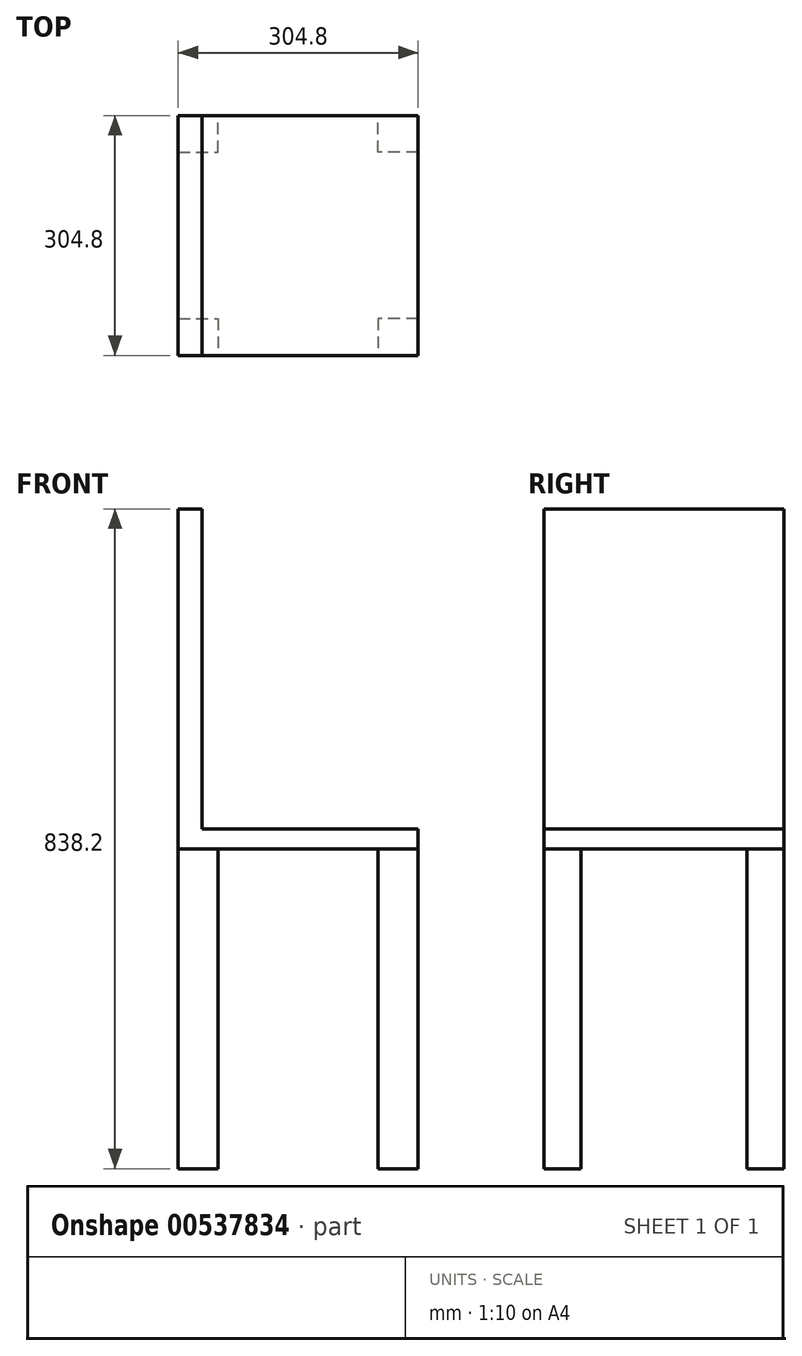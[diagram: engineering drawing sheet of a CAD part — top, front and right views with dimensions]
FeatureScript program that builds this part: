
annotation { "Feature Type Name" : "Feature", "Feature Type Description" : "" }
export const myFeature = defineFeature(function(context is Context, id is Id, definition is map)
    precondition{}
    {
        {
            var Q0;
            Q0=qCreatedBy(makeId("Top.planeOp"),FACE);
            var sketch = newSketch(context, id + "F0", { "sketchPlane" : qUnion([Q0])});
            skLineSegment(sketch, "E0", {"start": v(0, 0) * mm, "end": v(0, 46.95) * mm});
            skLineSegment(sketch, "E1", {"start": v(0, 46.95) * mm, "end": v(50.8, 46.95) * mm});
            skLineSegment(sketch, "E2", {"start": v(50.8, 46.95) * mm, "end": v(50.8, 0) * mm});
            skLineSegment(sketch, "E3", {"start": v(50.8, 0) * mm, "end": v(0, 0) * mm});
            skLineSegment(sketch, "E4", {"start": v(50.8, 0) * mm, "end": v(254, 0) * mm});
            skLineSegment(sketch, "E5", {"start": v(152.4, 0) * mm, "end": v(152.4, 304.8) * mm});
            skLineSegment(sketch, "E6.MirrorCS", {"start": v(254, 46.95) * mm, "end": v(254, 0) * mm});
            skLineSegment(sketch, "E7.MirrorCS", {"start": v(304.8, 46.95) * mm, "end": v(254, 46.95) * mm});
            skLineSegment(sketch, "E8.MirrorCS", {"start": v(304.8, 0) * mm, "end": v(304.8, 46.95) * mm});
            skLineSegment(sketch, "E9.MirrorCS", {"start": v(254, 0) * mm, "end": v(304.8, 0) * mm});
            skLineSegment(sketch, "E10", {"start": v(152.4, 152.4) * mm, "end": v(3.12, 152.4) * mm});
            skPoint(sketch, "E10.endSnap0", {"position": v(152.4, 152.4) * mm});
            skLineSegment(sketch, "E11.MirrorCS", {"start": v(0, 257.85) * mm, "end": v(50.8, 257.85) * mm});
            skLineSegment(sketch, "E12.MirrorCS", {"start": v(0, 304.8) * mm, "end": v(0, 257.85) * mm});
            skLineSegment(sketch, "E13.MirrorCS", {"start": v(50.8, 257.85) * mm, "end": v(50.8, 304.8) * mm});
            skLineSegment(sketch, "E14.MirrorCS", {"start": v(50.8, 304.8) * mm, "end": v(0, 304.8) * mm});
            skLineSegment(sketch, "E15.MirrorCS", {"start": v(304.8, 257.85) * mm, "end": v(254, 257.85) * mm});
            skLineSegment(sketch, "E16.MirrorCS", {"start": v(254, 257.85) * mm, "end": v(254, 304.8) * mm});
            skLineSegment(sketch, "E17.MirrorCS", {"start": v(304.8, 304.8) * mm, "end": v(304.8, 257.85) * mm});
            skLineSegment(sketch, "E18.MirrorCS", {"start": v(254, 304.8) * mm, "end": v(304.8, 304.8) * mm});
            skSolve(sketch);
        }
        {
            var Q0;
            Q0 = qSketchRegion(id + "F0", true);
            extrude(context, id + "F1", {"entities" : qUnion([Q0]), "depth" : 406.4 * mm, "offsetDistance" : 25.4 * mm});
        }
        {
            var Q0;
            Q0=makeQuery(id+"F1.opExtrude","CAP_FACE",FACE,{"disambiguationData":[OSD([sQuery(id+"F0.wireOp",EDGE,"E6.MirrorCS"),sQuery(id+"F0.wireOp",EDGE,"E7.MirrorCS"),sQuery(id+"F0.wireOp",EDGE,"E8.MirrorCS"),sQuery(id+"F0.wireOp",EDGE,"E9.MirrorCS")])],"isStart":false});
            var sketch = newSketch(context, id + "F2", { "sketchPlane" : qUnion([Q0])});
            skLineSegment(sketch, "E19.bottom", {"start": v(0, 0) * mm, "end": v(304.8, 0) * mm});
            skLineSegment(sketch, "E19.top", {"start": v(0, 304.8) * mm, "end": v(304.8, 304.8) * mm});
            skLineSegment(sketch, "E19.left", {"start": v(0, 0) * mm, "end": v(0, 304.8) * mm});
            skLineSegment(sketch, "E19.right", {"start": v(304.8, 0) * mm, "end": v(304.8, 304.8) * mm});
            skSolve(sketch);
        }
        {
            var Q0;
            Q0 = qSketchRegion(id + "F2", true);
            extrude(context, id + "F3", {"entities" : qUnion([Q0]), "depth" : 25.4 * mm, "offsetDistance" : 25.4 * mm});
        }
        {
            var Q0;
            Q0=makeQuery(id+"F3.opExtrude","CAP_FACE",FACE,{"disambiguationData":[OSD([sQuery(id+"F2.wireOp",EDGE,"E19.bottom"),sQuery(id+"F2.wireOp",EDGE,"E19.top"),sQuery(id+"F2.wireOp",EDGE,"E19.left"),sQuery(id+"F2.wireOp",EDGE,"E19.right")])],"isStart":false});
            var sketch = newSketch(context, id + "F4", { "sketchPlane" : qUnion([Q0])});
            skLineSegment(sketch, "E20.bottom", {"start": v(0, 0) * mm, "end": v(30.08, 0) * mm});
            skLineSegment(sketch, "E20.top", {"start": v(0, 304.8) * mm, "end": v(30.08, 304.8) * mm});
            skLineSegment(sketch, "E20.left", {"start": v(0, 0) * mm, "end": v(0, 304.8) * mm});
            skLineSegment(sketch, "E20.right", {"start": v(30.08, 0) * mm, "end": v(30.08, 304.8) * mm});
            skSolve(sketch);
        }
        {
            var Q0;
            Q0 = qSketchRegion(id + "F4", true);
            extrude(context, id + "F5", {"entities" : qUnion([Q0]), "operationType" : NewBodyOperationType.ADD, "depth" : 406.4 * mm, "offsetDistance" : 25.4 * mm});
        }
    });
